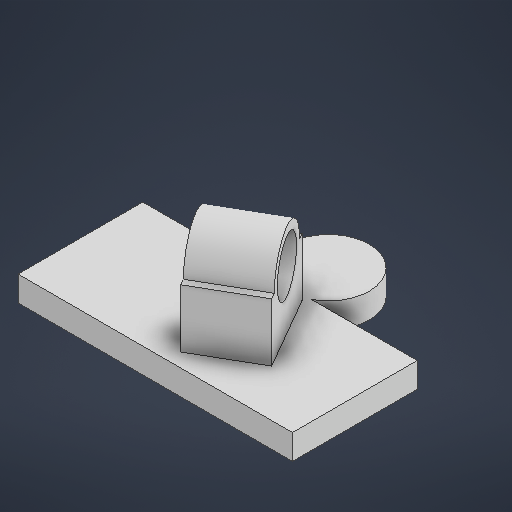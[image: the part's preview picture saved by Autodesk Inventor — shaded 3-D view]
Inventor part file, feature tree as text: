
AUTODESK INVENTOR PART (.ipt)
format: ipt  version: 2025.3 (Build 293356000, 356)  size: 223,232 bytes
history: native  units: in
note: dims shown in document units (in); Inventor stores cm internally (conversion verified against a paired STEP export)
features: other x3, extrude x1, sketch x1
ambient origin geometry x8: Origin, YZ Plane, XZ Plane, XY Plane, X Axis, Y Axis, Z Axis, Center Point
bodies: Solid1 (feature_tree)
feature tree (5):
  other  "Nozzle Fixer.ipt"
  extrude  "Extrusion1"  Depth=0.3937in
  other  "Solid1::Nozzle Fixer.ipt"
  other  "TaggingFeature1"
  sketch  "Sketch1"  dims[d0=0.3937in d1=0.1969in d2=0.0787in d3=0.3937in d4=0.0in]
